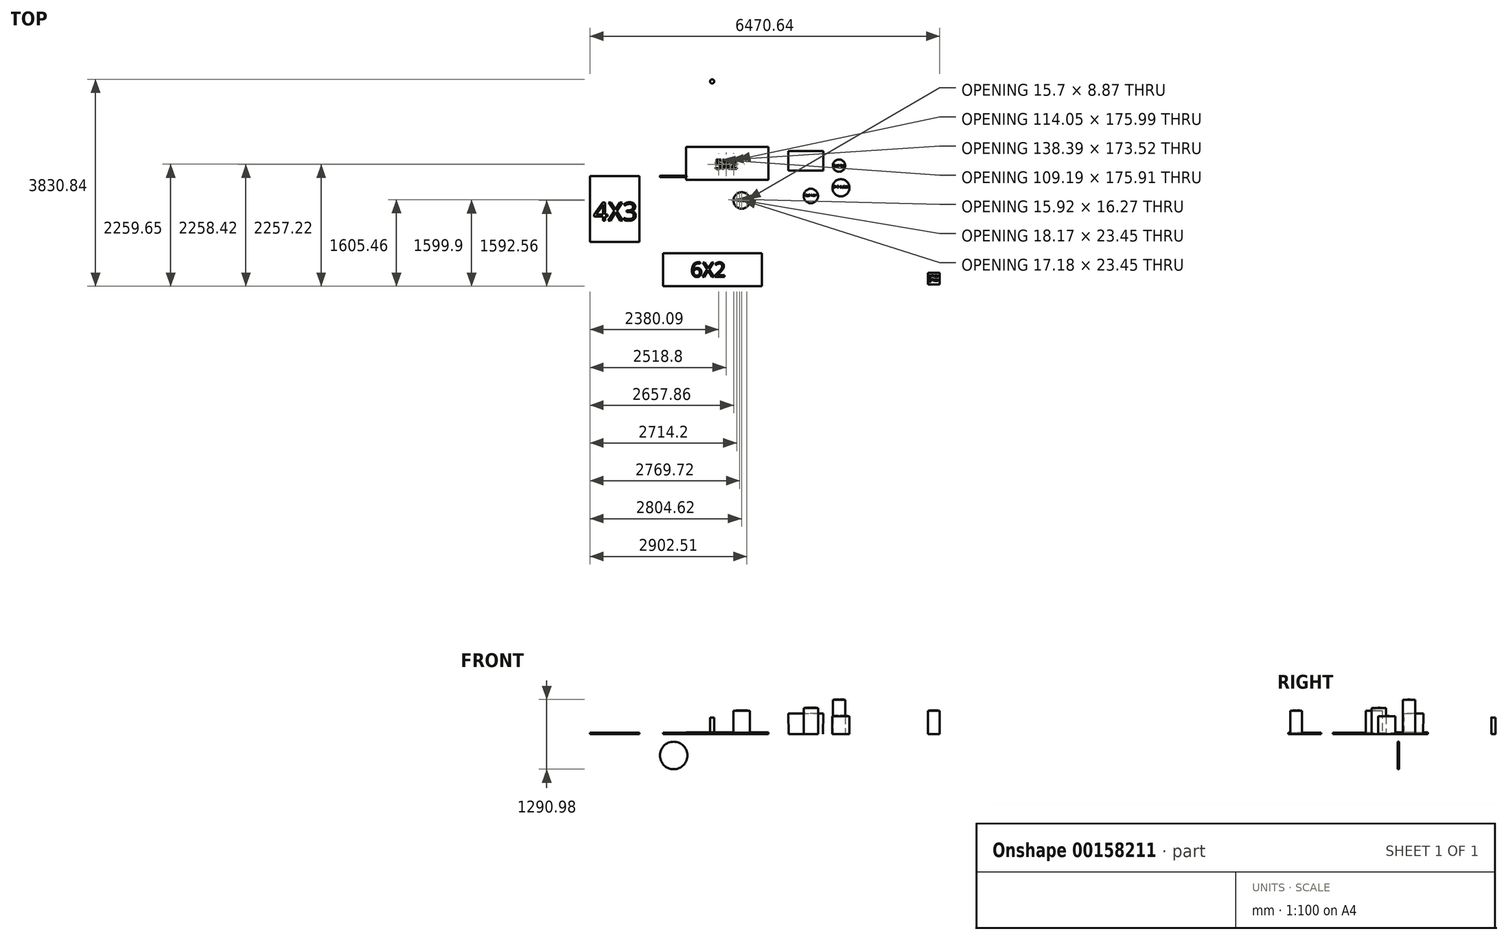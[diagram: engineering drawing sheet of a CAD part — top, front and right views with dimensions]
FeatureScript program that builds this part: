
annotation { "Feature Type Name" : "Feature", "Feature Type Description" : "" }
export const myFeature = defineFeature(function(context is Context, id is Id, definition is map)
    precondition{}
    {
        {
            var Q0;
            Q0=qCreatedBy(makeId("Top.planeOp"),FACE);
            var sketch = newSketch(context, id + "F0", { "sketchPlane" : qUnion([Q0])});
            skLineSegment(sketch, "E0.bottom", {"start": v(-3.5, 112.35) * mm, "end": v(-638.5, 112.35) * mm});
            skLineSegment(sketch, "E0.top", {"start": v(-3.5, 461.6) * mm, "end": v(-638.5, 461.6) * mm});
            skLineSegment(sketch, "E0.left", {"start": v(-3.5, 112.35) * mm, "end": v(-3.5, 461.6) * mm});
            skLineSegment(sketch, "E0.right", {"start": v(-638.5, 112.35) * mm, "end": v(-638.5, 461.6) * mm});
            skPoint(sketch, "E0.middle", {"position": v(-321, 286.98) * mm});
            skSolve(sketch);
        }
        {
            var Q0;
            Q0 = qSketchRegion(id + "F0", true);
            extrude(context, id + "F1", {"entities" : qUnion([Q0]), "depth" : 381 * mm, "hasDraft" : true, "draftAngle" : 1 * degree});
        }
        {
            var Q0;
            Q0=qCreatedBy(makeId("Top.planeOp"),FACE);
            var sketch = newSketch(context, id + "F2", { "sketchPlane" : qUnion([Q0])});
            skCircle(sketch, "E1", {"center": v(291.26, 198.92) * mm, "radius": 114.3 * mm});
            skSolve(sketch);
        }
        {
            var Q0;
            Q0 = qSketchRegion(id + "F2", true);
            extrude(context, id + "F3", {"entities" : qUnion([Q0]), "depth" : 635 * mm});
        }
        {
            var Q0;
            Q0=qCreatedBy(makeId("Top.planeOp"),FACE);
            var sketch = newSketch(context, id + "F4", { "sketchPlane" : qUnion([Q0])});
            skCircle(sketch, "E2", {"center": v(-228.8, -363.12) * mm, "radius": 133.35 * mm});
            skSolve(sketch);
        }
        {
            var Q0;
            Q0 = qSketchRegion(id + "F4", true);
            extrude(context, id + "F5", {"entities" : qUnion([Q0]), "depth" : 482.6 * mm});
        }
        {
            var Q0;
            Q0=qCreatedBy(makeId("Top.planeOp"),FACE);
            var sketch = newSketch(context, id + "F6", { "sketchPlane" : qUnion([Q0])});
            skCircle(sketch, "E3", {"center": v(328.04, -211.74) * mm, "radius": 158.75 * mm});
            skSolve(sketch);
        }
        {
            var Q0;
            Q0=makeQuery(id+"F6.imprint","IMPRINT",FACE,{"disambiguationData":[TD([[makeQuery(id+"F6.imprint","IMPRINT",EDGE,{"derivedFrom":sQuery(id+"F6.wireOp",EDGE,"E3")}),1.0]])]});
            extrude(context, id + "F7", {"entities" : qUnion([Q0]), "depth" : 330.2 * mm});
        }
        {
            var Q0;
            Q0=qCreatedBy(makeId("Top.planeOp"),FACE);
            var sketch = newSketch(context, id + "F8", { "sketchPlane" : qUnion([Q0])});
            skLineSegment(sketch, "E4.bottom", {"start": v(-1012.97, -62.7) * mm, "end": v(-2536.97, -62.7) * mm});
            skLineSegment(sketch, "E4.top", {"start": v(-1012.97, 546.9) * mm, "end": v(-2536.97, 546.9) * mm});
            skLineSegment(sketch, "E4.left", {"start": v(-1012.97, -62.7) * mm, "end": v(-1012.97, 546.9) * mm});
            skLineSegment(sketch, "E4.right", {"start": v(-2536.97, -62.7) * mm, "end": v(-2536.97, 546.9) * mm});
            skPoint(sketch, "E4.middle", {"position": v(-1774.97, 242.1) * mm});
            skSolve(sketch);
        }
        {
            var Q0;
            Q0=makeQuery(id+"F8.imprint","IMPRINT",FACE,{"disambiguationData":[TD([[makeQuery(id+"F8.imprint","IMPRINT",EDGE,{"derivedFrom":sQuery(id+"F8.wireOp",EDGE,"E4.bottom")}),-1.0]])]});
            extrude(context, id + "F9", {"entities" : qUnion([Q0]), "depth" : 25.4 * mm});
        }
        {
            var Q0;
            Q0=qCreatedBy(makeId("Top.planeOp"),FACE);
            var sketch = newSketch(context, id + "F10", { "sketchPlane" : qUnion([Q0])});
            skCircle(sketch, "E5", {"center": v(-1508.65, -446.3) * mm, "radius": 152.4 * mm});
            skSolve(sketch);
        }
        {
            var Q0;
            Q0 = qSketchRegion(id + "F10", true);
            extrude(context, id + "F11", {"entities" : qUnion([Q0]), "depth" : 431.8 * mm});
        }
        {
            var Q0;
            Q0=qCreatedBy(makeId("Top.planeOp"),FACE);
            var sketch = newSketch(context, id + "F12", { "sketchPlane" : qUnion([Q0])});
            skLineSegment(sketch, "E6.bottom", {"start": v(-3400.98, -1210.56) * mm, "end": v(-4315.38, -1210.56) * mm});
            skLineSegment(sketch, "E6.top", {"start": v(-3400.98, 8.64) * mm, "end": v(-4315.38, 8.64) * mm});
            skLineSegment(sketch, "E6.left", {"start": v(-3400.98, -1210.56) * mm, "end": v(-3400.98, 8.64) * mm});
            skLineSegment(sketch, "E6.right", {"start": v(-4315.38, -1210.56) * mm, "end": v(-4315.38, 8.64) * mm});
            skPoint(sketch, "E6.middle", {"position": v(-3858.18, -600.96) * mm});
            skSolve(sketch);
        }
        {
            var Q0;
            Q0=makeQuery(id+"F12.imprint","IMPRINT",FACE,{"disambiguationData":[TD([[makeQuery(id+"F12.imprint","IMPRINT",EDGE,{"derivedFrom":sQuery(id+"F12.wireOp",EDGE,"E6.bottom")}),-1.0]])]});
            extrude(context, id + "F13", {"entities" : qUnion([Q0]), "depth" : 25.4 * mm});
        }
        {
            var Q0;
            Q0=makeQuery(id+"F11.opExtrude","CAP_FACE",FACE,{"disambiguationData":[OSD([sQuery(id+"F10.wireOp",EDGE,"E5")])],"isStart":false});
            var sketch = newSketch(context, id + "F14", { "sketchPlane" : qUnion([Q0])});
            skText(sketch, "E7", { "text": "Propane\n", "fontName": "OpenSans-Regular.ttf"});
            const initialGuessF14  = {"E7": [-1.6193, -0.45747, 1, 0, 0.0404]};
            skSetInitialGuess(sketch, initialGuessF14);
            skSolve(sketch);
        }
        {
            var Q0;
            Q0 = qSketchRegion(id + "F14", true);
            var Q1;
            Q1=makeQuery(id+"F9.opExtrude","CAP_FACE",FACE,{"disambiguationData":[OSD([sQuery(id+"F8.wireOp",EDGE,"E4.bottom"),sQuery(id+"F8.wireOp",EDGE,"E4.top"),sQuery(id+"F8.wireOp",EDGE,"E4.left"),sQuery(id+"F8.wireOp",EDGE,"E4.right")])],"isStart":false});
            extrude(context, id + "F15", {"entities" : qUnion([Q0, Q1]), "depth" : 3.17 * mm});
        }
        {
            var Q0;
            Q0=makeQuery(id+"F5.opExtrude","CAP_FACE",FACE,{"disambiguationData":[OSD([sQuery(id+"F4.wireOp",EDGE,"E2")])],"isStart":false});
            var sketch = newSketch(context, id + "F16", { "sketchPlane" : qUnion([Q0])});
            skText(sketch, "E8", { "text": "5 gal Water\n", "fontName": "OpenSans-Regular.ttf"});
            const initialGuessF16  = {"E8": [-0.32869, -0.3615, 1, 0, 0.02759]};
            skSetInitialGuess(sketch, initialGuessF16);
            skSolve(sketch);
        }
        {
            var Q0;
            Q0 = qSketchRegion(id + "F16", true);
            extrude(context, id + "F17", {"entities" : qUnion([Q0]), "operationType" : NewBodyOperationType.ADD, "depth" : 3.17 * mm});
        }
        {
            var Q0;
            Q0=makeQuery(id+"F7.opExtrude","CAP_FACE",FACE,{"disambiguationData":[OSD([sQuery(id+"F6.wireOp",EDGE,"E3")])],"isStart":false});
            var sketch = newSketch(context, id + "F18", { "sketchPlane" : qUnion([Q0])});
            skText(sketch, "E9", { "text": "Swill bucket\n", "fontName": "OpenSans-Regular.ttf"});
            const initialGuessF18  = {"E9": [0.1953, -0.2073, 1, 0, 0.03419]};
            skSetInitialGuess(sketch, initialGuessF18);
            skSolve(sketch);
        }
        {
            var Q0;
            Q0 = qSketchRegion(id + "F18", true);
            extrude(context, id + "F19", {"entities" : qUnion([Q0]), "operationType" : NewBodyOperationType.ADD, "depth" : 3.17 * mm});
        }
        {
            var Q0;
            Q0=makeQuery(id+"F3.opExtrude","CAP_FACE",FACE,{"disambiguationData":[OSD([sQuery(id+"F2.wireOp",EDGE,"E1")])],"isStart":false});
            var sketch = newSketch(context, id + "F20", { "sketchPlane" : qUnion([Q0])});
            skText(sketch, "E10", { "text": "5 gal Keg\n", "fontName": "OpenSans-Regular.ttf"});
            const initialGuessF20  = {"E10": [0.2026, 0.18417, 1, 0, 0.0304]};
            skSetInitialGuess(sketch, initialGuessF20);
            skSolve(sketch);
        }
        {
            var Q0;
            Q0 = qSketchRegion(id + "F20", true);
            extrude(context, id + "F21", {"entities" : qUnion([Q0]), "operationType" : NewBodyOperationType.ADD, "depth" : 3.17 * mm});
        }
        {
            var Q0;
            Q0=makeQuery(id+"F1.opExtrude","CAP_FACE",FACE,{"disambiguationData":[OSD([sQuery(id+"F0.wireOp",EDGE,"E0.bottom"),sQuery(id+"F0.wireOp",EDGE,"E0.top"),sQuery(id+"F0.wireOp",EDGE,"E0.left"),sQuery(id+"F0.wireOp",EDGE,"E0.right")])],"isStart":false});
            var sketch = newSketch(context, id + "F22", { "sketchPlane" : qUnion([Q0])});
            skText(sketch, "E11", { "text": "KOOOLER\n", "fontName": "OpenSans-Regular.ttf"});
            const initialGuessF22  = {"E11": [-0.58804, 0.26337, 1, 0, 0.08117]};
            skSetInitialGuess(sketch, initialGuessF22);
            skSolve(sketch);
        }
        {
            var Q0;
            Q0 = qConstructionFilter(qBodyType(qCreatedBy(id + "F22" ,EDGE), BodyType.WIRE), ConstructionObject.NO);
            extrude(context, id + "F23", {"bodyType" : ToolBodyType.SURFACE, "surfaceEntities" : qUnion([Q0]), "depth" : 3.17 * mm});
        }
        {
            var Q0;
            Q0=makeQuery(id+"F13.opExtrude","CAP_FACE",FACE,{"disambiguationData":[OSD([sQuery(id+"F12.wireOp",EDGE,"E6.bottom"),sQuery(id+"F12.wireOp",EDGE,"E6.top"),sQuery(id+"F12.wireOp",EDGE,"E6.left"),sQuery(id+"F12.wireOp",EDGE,"E6.right")])],"isStart":false});
            var sketch = newSketch(context, id + "F24", { "sketchPlane" : qUnion([Q0])});
            skText(sketch, "E12", { "text": "4X3", "fontName": "OpenSans-Regular.ttf"});
            const initialGuessF24  = {"E12": [-4.24843, -0.81783, 1, 0, 0.33738]};
            skSetInitialGuess(sketch, initialGuessF24);
            skSolve(sketch);
        }
        {
            var Q0;
            Q0 = qSketchRegion(id + "F24", true);
            extrude(context, id + "F25", {"entities" : qUnion([Q0]), "operationType" : NewBodyOperationType.REMOVE, "oppositeDirection" : true, "depth" : 0.64 * mm});
        }
        {
            var Q0;
            Q0=makeQuery(id+"F15.opExtrude","CAP_FACE",FACE,{"disambiguationData":[OSD([sQuery(id+"F8.wireOp",EDGE,"E4.bottom"),sQuery(id+"F8.wireOp",EDGE,"E4.top"),sQuery(id+"F8.wireOp",EDGE,"E4.left"),sQuery(id+"F8.wireOp",EDGE,"E4.right")])],"isStart":false});
            var sketch = newSketch(context, id + "F26", { "sketchPlane" : qUnion([Q0])});
            skText(sketch, "E13", { "text": "5X2\n", "fontName": "OpenSans-Regular.ttf"});
            const initialGuessF26  = {"E13": [-2.00568, 0.13662, 1, 0, 0.175]};
            skSetInitialGuess(sketch, initialGuessF26);
            skSolve(sketch);
        }
        {
            var Q0;
            Q0 = qSketchRegion(id + "F26", true);
            extrude(context, id + "F27", {"entities" : qUnion([Q0]), "operationType" : NewBodyOperationType.REMOVE, "oppositeDirection" : true, "depth" : 3.17 * mm});
        }
        {
            var Q0;
            Q0=qCreatedBy(makeId("Top.planeOp"),FACE);
            var sketch = newSketch(context, id + "F28", { "sketchPlane" : qUnion([Q0])});
            skLineSegment(sketch, "E14.bottom", {"start": v(-2966.64, -2035.04) * mm, "end": v(-1137.84, -2035.04) * mm});
            skLineSegment(sketch, "E14.top", {"start": v(-2966.64, -1425.44) * mm, "end": v(-1137.84, -1425.44) * mm});
            skLineSegment(sketch, "E14.left", {"start": v(-2966.64, -2035.04) * mm, "end": v(-2966.64, -1425.44) * mm});
            skLineSegment(sketch, "E14.right", {"start": v(-1137.84, -2035.04) * mm, "end": v(-1137.84, -1425.44) * mm});
            skSolve(sketch);
        }
        {
            var Q0;
            Q0 = qSketchRegion(id + "F28", true);
            extrude(context, id + "F29", {"entities" : qUnion([Q0]), "depth" : 25.4 * mm});
        }
        {
            var Q0;
            Q0=makeQuery(id+"F29.opExtrude","CAP_FACE",FACE,{"disambiguationData":[OSD([sQuery(id+"F28.wireOp",EDGE,"E14.bottom"),sQuery(id+"F28.wireOp",EDGE,"E14.top"),sQuery(id+"F28.wireOp",EDGE,"E14.left"),sQuery(id+"F28.wireOp",EDGE,"E14.right")])],"isStart":false});
            var sketch = newSketch(context, id + "F30", { "sketchPlane" : qUnion([Q0])});
            skText(sketch, "E15", { "text": "6X2\n", "fontName": "OpenSans-Regular.ttf"});
            const initialGuessF30  = {"E15": [-2.45149, -1.86022, 1, 0, 0.26972]};
            skSetInitialGuess(sketch, initialGuessF30);
            skSolve(sketch);
        }
        {
            var Q0;
            Q0 = qSketchRegion(id + "F30", true);
            extrude(context, id + "F31", {"entities" : qUnion([Q0]), "operationType" : NewBodyOperationType.REMOVE, "oppositeDirection" : true, "depth" : 3.17 * mm});
        }
        {
            var Q0;
            Q0=qCreatedBy(makeId("Top.planeOp"),FACE);
            var sketch = newSketch(context, id + "F32", { "sketchPlane" : qUnion([Q0])});
            skLineSegment(sketch, "E16.bottom", {"start": v(1939.36, -1782.3) * mm, "end": v(2155.26, -1782.3) * mm});
            skLineSegment(sketch, "E16.top", {"start": v(1939.36, -1998.2) * mm, "end": v(2155.26, -1998.2) * mm});
            skLineSegment(sketch, "E16.left", {"start": v(1939.36, -1782.3) * mm, "end": v(1939.36, -1998.2) * mm});
            skLineSegment(sketch, "E16.right", {"start": v(2155.26, -1782.3) * mm, "end": v(2155.26, -1998.2) * mm});
            skSolve(sketch);
        }
        {
            var Q0;
            Q0 = qSketchRegion(id + "F32", true);
            extrude(context, id + "F33", {"entities" : qUnion([Q0]), "depth" : 431.8 * mm});
        }
        {
            var Q0;
            Q0=makeQuery(id+"F33.opExtrude","CAP_FACE",FACE,{"disambiguationData":[OSD([sQuery(id+"F32.wireOp",EDGE,"E16.bottom"),sQuery(id+"F32.wireOp",EDGE,"E16.top"),sQuery(id+"F32.wireOp",EDGE,"E16.left"),sQuery(id+"F32.wireOp",EDGE,"E16.right")])],"isStart":false});
            var sketch = newSketch(context, id + "F34", { "sketchPlane" : qUnion([Q0])});
            skText(sketch, "E17", { "text": "grinda\ngrinda\n", "fontName": "OpenSans-Regular.ttf"});
            const initialGuessF34  = {"E17": [1.9615, -1.86401, 1, 0, 0.0397]};
            skSetInitialGuess(sketch, initialGuessF34);
            skSolve(sketch);
        }
        {
            var Q0;
            Q0 = qSketchRegion(id + "F34", true);
            extrude(context, id + "F35", {"entities" : qUnion([Q0]), "operationType" : NewBodyOperationType.ADD, "depth" : 6.35 * mm});
        }
        {
            var Q0;
            Q0=qCreatedBy(makeId("Top.planeOp"),FACE);
            var sketch = newSketch(context, id + "F36", { "sketchPlane" : qUnion([Q0])});
            skCircle(sketch, "E18", {"center": v(-2056.4, 1757.7) * mm, "radius": 38.1 * mm});
            skSolve(sketch);
        }
        {
            var Q0;
            Q0 = qSketchRegion(id + "F36", true);
            extrude(context, id + "F37", {"entities" : qUnion([Q0]), "depth" : 304.8 * mm});
        }
        {
            var Q0;
            Q0=qCreatedBy(makeId("Front.planeOp"),FACE);
            var sketch = newSketch(context, id + "F38", { "sketchPlane" : qUnion([Q0])});
            skCircle(sketch, "E19", {"center": v(-2768.52, -398.8) * mm, "radius": 254 * mm});
            skSolve(sketch);
        }
        {
            var Q0;
            Q0 = qSketchRegion(id + "F38", true);
            extrude(context, id + "F39", {"entities" : qUnion([Q0]), "endBound" : BoundingType.SYMMETRIC, "depth" : 25.4 * mm});
        }
        {
            var Q0;
            Q0=makeQuery(id+"F39.opExtrude","CAP_FACE",FACE,{"disambiguationData":[OSD([sQuery(id+"F38.wireOp",EDGE,"E19")])],"isStart":true});
            var Q1;
            Q1=makeQuery(id+"F39.opExtrude","CAP_FACE",FACE,{"disambiguationData":[OSD([sQuery(id+"F38.wireOp",EDGE,"E19")])],"isStart":false});
            fillet(context, id + "F40", {"entities" : qUnion([Q0, Q1]), "radius" : 9.52 * mm, "tangentPropagation" : true, "allowEdgeOverflow" : false});
        }
    });
